# Revit family: Grundplatten Typ V
name_source: partatom
category: HLS-Bauteile
revit_build: Autodesk Revit 2017 (Build: 20190507_1515(x64)
units: mm (PartAtom-declared; Revit-internal decimal feet)

## family parameters
Arbeitsebenenbasiert = Ja
Beim Laden mit Abzugskörper schneiden = Nein
Bemaßung runder Anschluss = Durchmesser verwenden
Gemeinsam genutzt = Ja
Immer vertikal = Nein
Raumberechnungspunkt = Nein
Teiletyp = Normal

## types (3) — shared parameters
Abmessung = 120 x 40 x 5 mm
Anzahl Befestigungsloch = 2
B = 40 mm  [stored 0.131234 ft]
Breite = 40 mm  [stored 0.131234 ft]
D = 13 mm  [stored 0.0426509 ft]
Fabrikat = MEFA
Firma = MEFA Befestigungs- und Montagesysteme GmbH
Kurztext1 = Grundplatte Typ V
L = 120 mm  [stored 0.393701 ft]
L1 = 75 mm
Lochabstand längs = 75 mm
Lochdurchmesser = 13 mm
Länge = 120 mm  [stored 0.393701 ft]
MD = 5 mm  [stored 0.0164042 ft]
Material = Stahl
Materialname = S235
Mengeneinheit = St
Oberflaeche = galvanisch verzinkt
Stärke = 5 mm  [stored 0.0164042 ft]
Vorgabe-Ansicht = 1219 mm
max. zul. Last hängend = 2.70 kN
vpe = 50 St
zero-valued in all types: Sicherheitsfaktor

## per-type parameters (varying)
| type | Anschluss | Artikelnummer | EAN | Gewicht | Gewicht pro Bauteil | HGA | Kurztext2 | Runde Gewindeanschluss |
| Grundplatten Typ V 120x40x5,0 1/2" | 1/2'' | 0590586 | 4250928415271 | 0.21 kg | 0.21 kg | 15 mm  [stored 0.0492126 ft] | Anschluss 1/2'' Platte 120x40x5 mm | Runde Gewindeanschlusse parametrik : Muffe 1/2´´ (0009865) |
| Grundplatten Typ V 120x40x5,0 3/4" | 3/4'' | 0590587 | 4250928415288 | 0.23 kg | 0.23 kg | 17 mm | Anschluss 3/4'' Platte 120x40x5 mm | Runde Gewindeanschlusse parametrik : Schweißmuffe 3/4´´ (0009873) |
| Grundplatten Typ V 120x40x5,0 1" | 1'' | 0590588 | 4250928415295 | 0.26 kg | 0.26 kg | 20 mm  [stored 0.0656168 ft] | Anschluss 1'' Platte 120x40x5 mm | Runde Gewindeanschlusse parametrik : Muffe 1´´ (0009881) |

note: [stored X ft] marks values corroborated as IEEE doubles in the binary element streams (Revit-internal decimal feet)

## geometry (parser evidence)
native form markers: Sweep x3
no freeform markers — native parametric forms only
